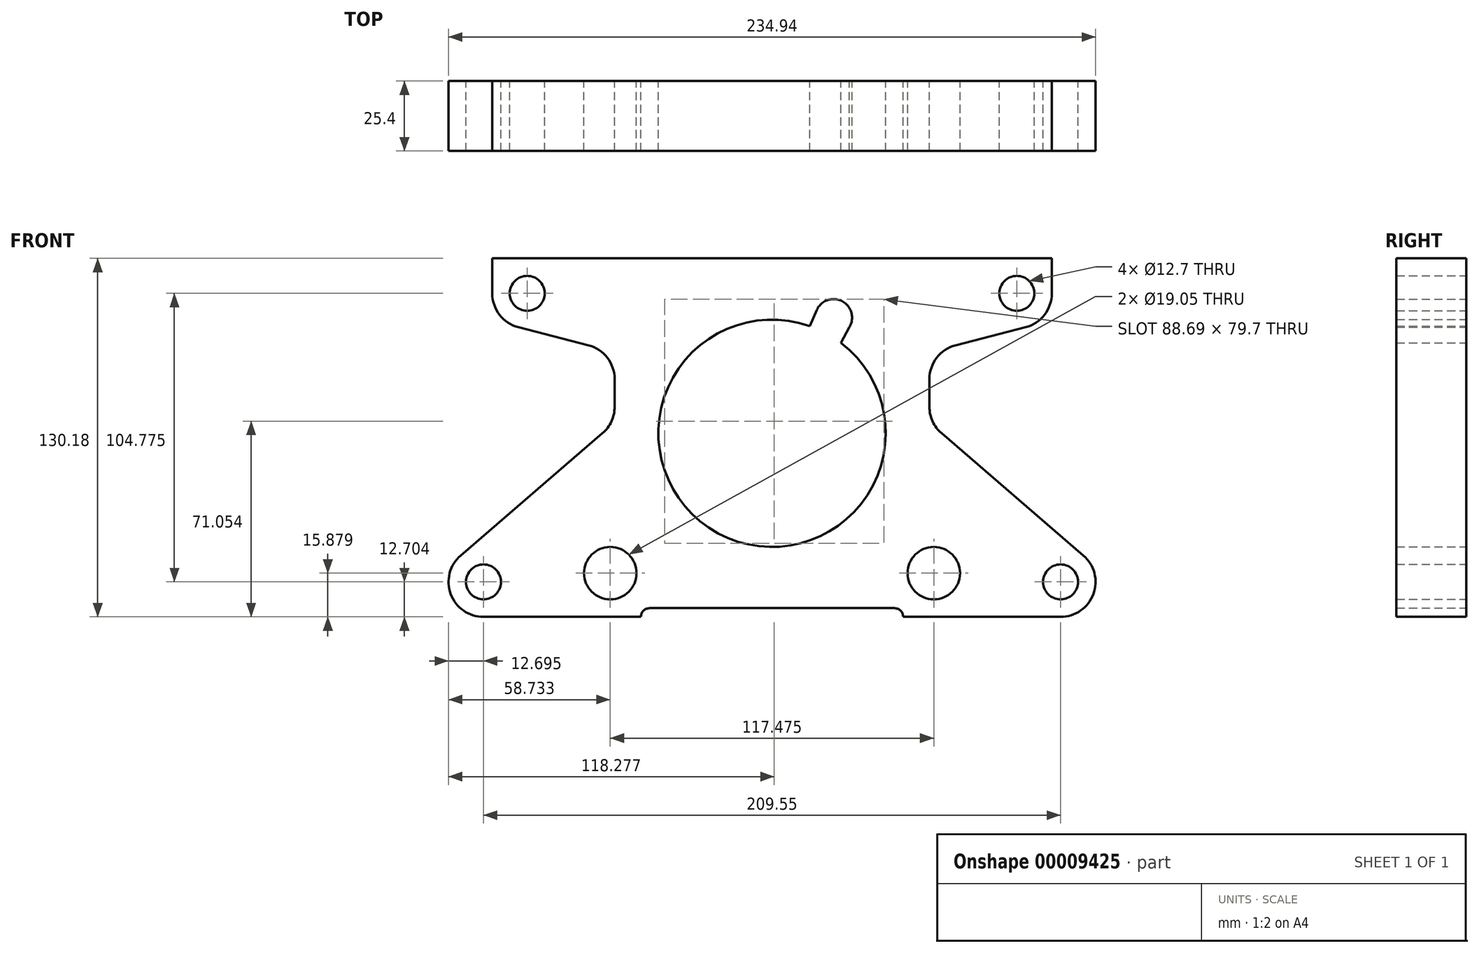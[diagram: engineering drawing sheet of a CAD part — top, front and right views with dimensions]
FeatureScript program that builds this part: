
annotation { "Feature Type Name" : "Feature", "Feature Type Description" : "" }
export const myFeature = defineFeature(function(context is Context, id is Id, definition is map)
    precondition{}
    {
        {
            var Q0;
            Q0=qCreatedBy(makeId("Front.planeOp"),FACE);
            var sketch = newSketch(context, id + "F0", { "sketchPlane" : qUnion([Q0])});
            skLineSegment(sketch, "E0", {"start": v(-101.6, 25) * mm, "end": v(0, 25) * mm});
            skLineSegment(sketch, "E1", {"start": v(-101.6, 25) * mm, "end": v(-101.6, 12.3) * mm});
            skLineSegment(sketch, "E2", {"start": v(-92.07, 0) * mm, "end": v(-66.68, -6.54) * mm});
            skLineSegment(sketch, "E3", {"start": v(-57.15, -18.84) * mm, "end": v(-57.15, -28.88) * mm});
            skLineSegment(sketch, "E4", {"start": v(-104.78, -105.18) * mm, "end": v(-47.63, -105.18) * mm});
            skLineSegment(sketch, "E5", {"start": v(-47.63, -105.18) * mm, "end": v(-47.63, -105.18) * mm});
            skLineSegment(sketch, "E6", {"start": v(-44.45, -102) * mm, "end": v(0, -102) * mm});
            skArc(sketch, "E7", {"start": v(-104.78, -105.18) * mm, "mid": v(-116.68, -96.9) * mm, "end": v(-113.06, -82.85) * mm});
            skLineSegment(sketch, "E8", {"start": v(-61.56, -38.5) * mm, "end": v(-113.06, -82.85) * mm});
            skPoint(sketch, "E9.orphan", {"position": v(-104.78, -79.78) * mm});
            skPoint(sketch, "E10.visualSharp", {"position": v(-57.15, -34.7) * mm});
            skArc(sketch, "E10.filletArc", {"start": v(-61.56, -38.5) * mm, "mid": v(-58.3, -34.17) * mm, "end": v(-57.15, -28.88) * mm});
            skPoint(sketch, "E11.visualSharp", {"position": v(-57.15, -9) * mm});
            skArc(sketch, "E11.filletArc", {"start": v(-57.15, -18.84) * mm, "mid": v(-59.81, -11.06) * mm, "end": v(-66.68, -6.54) * mm});
            skPoint(sketch, "E12.visualSharp", {"position": v(-101.6, 2.46) * mm});
            skArc(sketch, "E12.filletArc", {"start": v(-101.6, 12.3) * mm, "mid": v(-98.94, 4.52) * mm, "end": v(-92.07, 0) * mm});
            skPoint(sketch, "E13.visualSharp", {"position": v(-47.63, -102) * mm});
            skArc(sketch, "E13.filletArc", {"start": v(-44.45, -102) * mm, "mid": v(-46.7, -102.93) * mm, "end": v(-47.63, -105.18) * mm});
            skCircle(sketch, "E14", {"center": v(-104.78, -92.48) * mm, "radius": 6.35 * mm});
            skCircle(sketch, "E15", {"center": v(-58.74, -89.3) * mm, "radius": 9.53 * mm});
            skCircle(sketch, "E16", {"center": v(-88.9, 12.3) * mm, "radius": 6.35 * mm});
            skArc(sketch, "E17.0.MirrorCS", {"start": v(44.45, -102) * mm, "mid": v(46.7, -102.93) * mm, "end": v(47.63, -105.18) * mm});
            skArc(sketch, "E17.1.MirrorCS", {"start": v(57.15, -18.84) * mm, "mid": v(59.81, -11.06) * mm, "end": v(66.68, -6.54) * mm});
            skArc(sketch, "E17.2.MirrorCS", {"start": v(101.6, 12.3) * mm, "mid": v(98.94, 4.52) * mm, "end": v(92.07, 0) * mm});
            skArc(sketch, "E17.3.MirrorCS", {"start": v(61.56, -38.5) * mm, "mid": v(58.3, -34.17) * mm, "end": v(57.15, -28.88) * mm});
            skLineSegment(sketch, "E17.4.MirrorCS", {"start": v(101.6, 25) * mm, "end": v(101.6, 12.3) * mm});
            skCircle(sketch, "E17.5.MirrorC", {"center": v(88.9, 12.3) * mm, "radius": 6.35 * mm});
            skPoint(sketch, "E17.6.MirrorP", {"position": v(57.15, -34.7) * mm});
            skLineSegment(sketch, "E17.7.MirrorCS", {"start": v(101.6, 25) * mm, "end": v(0, 25) * mm});
            skCircle(sketch, "E17.8.MirrorC", {"center": v(58.74, -89.3) * mm, "radius": 9.53 * mm});
            skPoint(sketch, "E17.9.MirrorP", {"position": v(104.78, -79.78) * mm});
            skLineSegment(sketch, "E17.10.MirrorCS", {"start": v(104.78, -105.18) * mm, "end": v(47.63, -105.18) * mm});
            skLineSegment(sketch, "E17.11.MirrorCS", {"start": v(44.45, -102) * mm, "end": v(0, -102) * mm});
            skLineSegment(sketch, "E17.12.MirrorCS", {"start": v(92.07, 0) * mm, "end": v(66.68, -6.54) * mm});
            skPoint(sketch, "E17.13.MirrorP", {"position": v(47.63, -102) * mm});
            skArc(sketch, "E17.14.MirrorCS", {"start": v(104.78, -105.18) * mm, "mid": v(116.68, -96.9) * mm, "end": v(113.06, -82.85) * mm});
            skCircle(sketch, "E17.15.MirrorC", {"center": v(104.78, -92.48) * mm, "radius": 6.35 * mm});
            skLineSegment(sketch, "E17.16.MirrorCS", {"start": v(57.15, -18.84) * mm, "end": v(57.15, -28.88) * mm});
            skLineSegment(sketch, "E17.17.MirrorCS", {"start": v(61.56, -38.5) * mm, "end": v(113.06, -82.85) * mm});
            skPoint(sketch, "E17.18.MirrorP", {"position": v(57.15, -9) * mm});
            skLineSegment(sketch, "E17.19.MirrorCS", {"start": v(47.63, -105.18) * mm, "end": v(47.63, -105.18) * mm});
            skPoint(sketch, "E17.20.MirrorP", {"position": v(101.6, 2.46) * mm});
            skArc(sketch, "E18", {"start": v(13.66, 0.45) * mm, "mid": v(-19.58, -74.84) * mm, "end": v(25.02, -5.67) * mm});
            skLineSegment(sketch, "E19", {"start": v(0, -38.5) * mm, "end": v(52.12, 59.52) * mm, "construction": true});
            skArc(sketch, "E20", {"start": v(43.5, -19.1) * mm, "mid": v(27.62, 0.3) * mm, "end": v(4.09, 8.95) * mm, "construction": true});
            skArc(sketch, "E21", {"start": v(28.03, 0) * mm, "mid": v(25.5, 9.46) * mm, "end": v(16.24, 6.27) * mm});
            skLineSegment(sketch, "E22", {"start": v(16.24, 6.27) * mm, "end": v(13.66, 0.45) * mm});
            skLineSegment(sketch, "E23", {"start": v(28.03, 0) * mm, "end": v(25.02, -5.67) * mm});
            skSolve(sketch);
        }
        {
            var Q0;
            Q0=makeQuery(id+"F0.imprint","IMPRINT",FACE,{"disambiguationData":[TD([[makeQuery(id+"F0.imprint","IMPRINT",EDGE,{"derivedFrom":sQuery(id+"F0.wireOp",EDGE,"E0")}),-1.0]])]});
            extrude(context, id + "F1", {"entities" : qUnion([Q0]), "depth" : 25.4 * mm});
        }
    });
